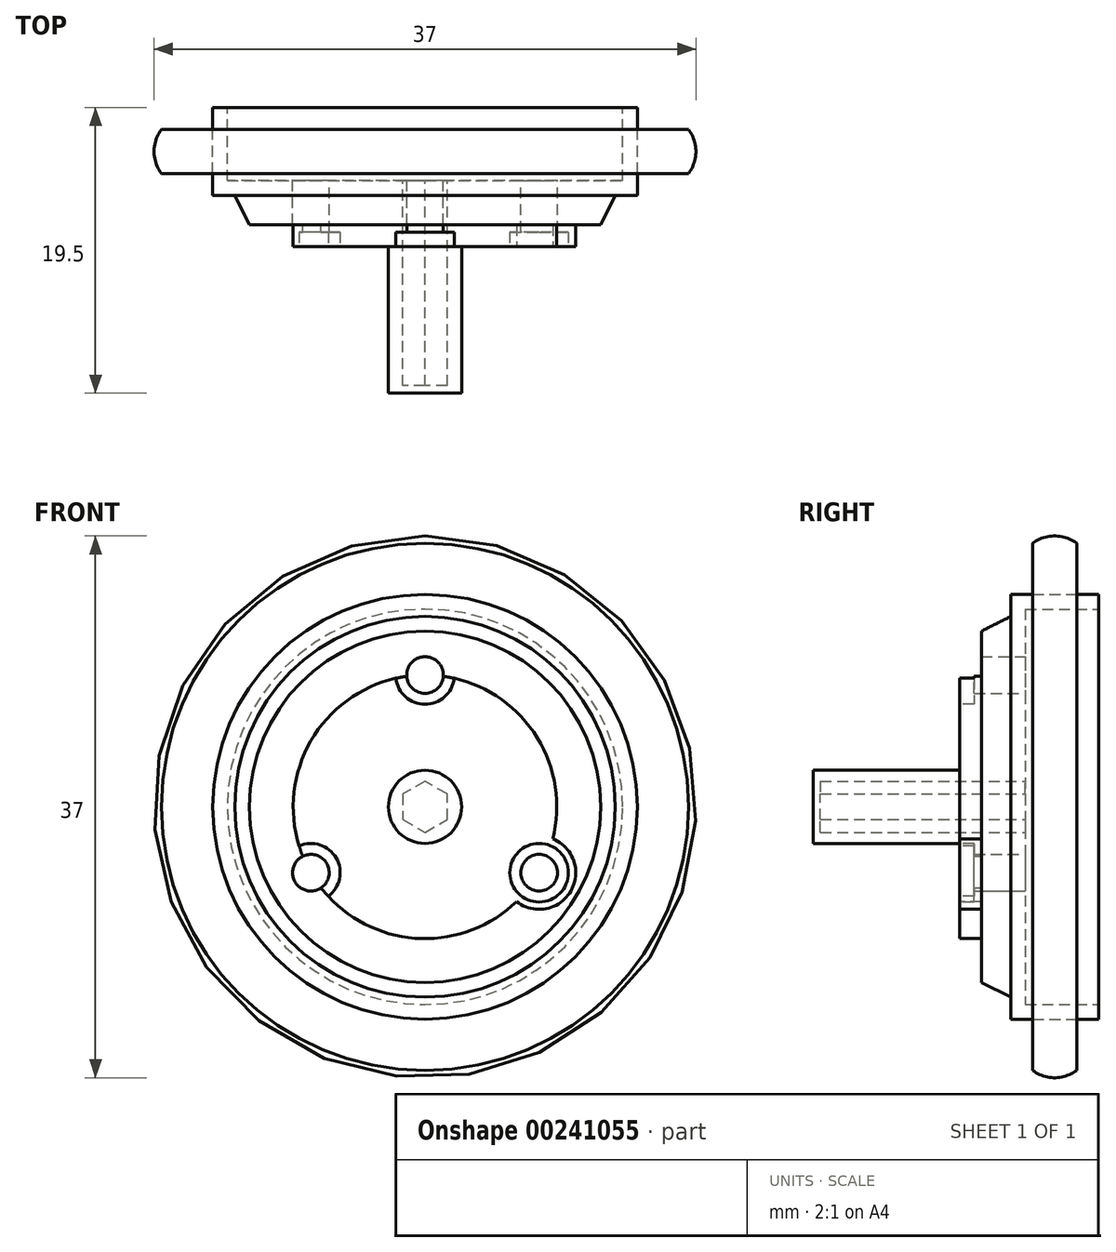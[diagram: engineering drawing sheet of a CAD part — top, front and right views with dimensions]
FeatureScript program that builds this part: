
annotation { "Feature Type Name" : "Feature", "Feature Type Description" : "" }
export const myFeature = defineFeature(function(context is Context, id is Id, definition is map)
    precondition{}
    {
        {
            var Q0;
            Q0=qCreatedBy(makeId("Front.planeOp"),FACE);
            var sketch = newSketch(context, id + "F0", { "sketchPlane" : qUnion([Q0])});
            skCircle(sketch, "E0", {"center": v(0, 0) * mm, "radius": 14.5 * mm});
            skSolve(sketch);
        }
        {
            var Q0;
            Q0=makeQuery(id+"F0.imprint","IMPRINT",FACE,{"disambiguationData":[TD([[makeQuery(id+"F0.imprint","IMPRINT",EDGE,{"derivedFrom":sQuery(id+"F0.wireOp",EDGE,"E0")}),1.0]])]});
            extrude(context, id + "F1", {"entities" : qUnion([Q0]), "depth" : 6 * mm});
        }
        {
            var Q0;
            Q0=qCreatedBy(makeId("Right.planeOp"),FACE);
            var sketch = newSketch(context, id + "F2", { "sketchPlane" : qUnion([Q0])});
            skLineSegment(sketch, "E1.0", {"start": v(-6, -14.5) * mm, "end": v(-6, 14.5) * mm, "construction": true});
            skLineSegment(sketch, "E2", {"start": v(-6, 0) * mm, "end": v(-8, 0) * mm});
            skPoint(sketch, "E2.endSnap0", {"position": v(-6, 0) * mm});
            skLineSegment(sketch, "E3", {"start": v(-8, 0) * mm, "end": v(-8, 12) * mm});
            skLineSegment(sketch, "E4", {"start": v(-8, 12) * mm, "end": v(-6, 13) * mm});
            skLineSegment(sketch, "E5", {"start": v(-6, 13) * mm, "end": v(-6, 0) * mm});
            skSolve(sketch);
        }
        {
            var Q0;
            Q0=makeQuery(id+"F2.imprint","IMPRINT",FACE,{"disambiguationData":[TD([[makeQuery(id+"F2.imprint","IMPRINT",EDGE,{"derivedFrom":sQuery(id+"F2.wireOp",EDGE,"E2")}),-1.0]])]});
            var Q1;
            Q1=sQuery(id+"F2.wireOp",EDGE,"E2");
            revolve(context, id + "F3", {"operationType" : NewBodyOperationType.ADD, "entities" : qUnion([Q0]), "axis" : qUnion([Q1]), "revolveType" : RevolveType.FULL});
        }
        {
            var Q0;
            Q0=makeQuery(id+"F3.opRevolve","SWEPT_FACE",FACE,{"disambiguationData":[OSD([sQuery(id+"F2.wireOp",EDGE,"E3")])]});
            var sketch = newSketch(context, id + "F4", { "sketchPlane" : qUnion([Q0])});
            skCircle(sketch, "E6", {"center": v(0, 0) * mm, "radius": 9 * mm});
            skSolve(sketch);
        }
        {
            var Q0;
            Q0=makeQuery(id+"F4.imprint","IMPRINT",FACE,{"disambiguationData":[TD([[makeQuery(id+"F4.imprint","IMPRINT",EDGE,{"derivedFrom":sQuery(id+"F4.wireOp",EDGE,"E6")}),1.0]])]});
            extrude(context, id + "F5", {"entities" : qUnion([Q0]), "operationType" : NewBodyOperationType.ADD, "depth" : 1.5 * mm});
        }
        {
            var Q0;
            Q0=makeQuery(id+"F5.opExtrude","CAP_FACE",FACE,{"disambiguationData":[OSD([sQuery(id+"F4.wireOp",EDGE,"E6")])],"isStart":false});
            var sketch = newSketch(context, id + "F6", { "sketchPlane" : qUnion([Q0])});
            skCircle(sketch, "E7", {"center": v(0, 0) * mm, "radius": 2.5 * mm});
            skSolve(sketch);
        }
        {
            var Q0;
            Q0=makeQuery(id+"F6.imprint","IMPRINT",FACE,{"disambiguationData":[TD([[makeQuery(id+"F6.imprint","IMPRINT",EDGE,{"derivedFrom":sQuery(id+"F6.wireOp",EDGE,"E7")}),1.0]])]});
            extrude(context, id + "F7", {"entities" : qUnion([Q0]), "operationType" : NewBodyOperationType.ADD, "depth" : 10 * mm});
        }
        {
            var Q0;
            Q0=makeQuery(id+"F5.opExtrude","CAP_FACE",FACE,{"disambiguationData":[OSD([sQuery(id+"F4.wireOp",EDGE,"E6")])],"isStart":false});
            var sketch = newSketch(context, id + "F8", { "sketchPlane" : qUnion([Q0])});
            skCircle(sketch, "E8.0", {"center": v(0, 0) * mm, "radius": 9 * mm, "construction": true});
            skLineSegment(sketch, "E9.0", {"start": v(0, 9) * mm, "end": v(7.8, -4.5) * mm});
            skLineSegment(sketch, "E9.1", {"start": v(7.8, -4.5) * mm, "end": v(-7.8, -4.5) * mm});
            skLineSegment(sketch, "E9.2", {"start": v(-7.8, -4.5) * mm, "end": v(0, 9) * mm});
            skCircle(sketch, "E10", {"center": v(0, 9) * mm, "radius": 2.5 * mm});
            skCircle(sketch, "E11", {"center": v(7.8, -4.5) * mm, "radius": 2.5 * mm});
            skCircle(sketch, "E12", {"center": v(-7.8, -4.5) * mm, "radius": 2.5 * mm});
            skSolve(sketch);
        }
        {
            var Q0;
            {var subQ0=sQuery(id+"F8.wireOp",EDGE,"E9.0");var subQ3=sQuery(id+"F8.wireOp",EDGE,"E11");var subQ4=makeQuery(id+"F8.imprint","INTERSECT",VERTEX,{"derivedFrom":[subQ0,subQ3]});Q0=makeQuery(id+"F8.imprint","IMPRINT",FACE,{"disambiguationData":[TD([[makeQuery(id+"F8.imprint","IMPRINT",EDGE,{"disambiguationData":[TD([[subQ4,1.0]])],"derivedFrom":subQ3}),1.0]])]});}
            var Q1;
            {var subQ0=sQuery(id+"F8.wireOp",EDGE,"E11");var subQ1=makeQuery(id+"F5.opExtrude","CAP_EDGE",EDGE,{"disambiguationData":[OSD([sQuery(id+"F4.wireOp",EDGE,"E6")])],"isStart":false});var subQ2=makeQuery(id+"F8.imprint","INTERSECT",VERTEX,{"disambiguationData":[OD(0.0)],"derivedFrom":[subQ1,subQ0]});Q1=makeQuery(id+"F8.imprint","IMPRINT",FACE,{"disambiguationData":[TD([[makeQuery(id+"F8.imprint","IMPRINT",EDGE,{"disambiguationData":[TD([[subQ2,1.0]])],"derivedFrom":subQ0}),1.0]])]});}
            var Q2;
            {var subQ0=sQuery(id+"F8.wireOp",EDGE,"E9.1");var subQ3=sQuery(id+"F8.wireOp",EDGE,"E11");var subQ4=makeQuery(id+"F8.imprint","INTERSECT",VERTEX,{"derivedFrom":[subQ0,subQ3]});Q2=makeQuery(id+"F8.imprint","IMPRINT",FACE,{"disambiguationData":[TD([[makeQuery(id+"F8.imprint","IMPRINT",EDGE,{"disambiguationData":[TD([[subQ4,-1.0]])],"derivedFrom":subQ3}),1.0]])]});}
            var Q3;
            {var subQ1=sQuery(id+"F8.wireOp",EDGE,"E9.0");var subQ3=sQuery(id+"F8.wireOp",EDGE,"E11");var subQ4=makeQuery(id+"F8.imprint","INTERSECT",VERTEX,{"derivedFrom":[subQ1,subQ3]});Q3=makeQuery(id+"F8.imprint","IMPRINT",FACE,{"disambiguationData":[TD([[makeQuery(id+"F8.imprint","IMPRINT",EDGE,{"disambiguationData":[TD([[subQ4,-1.0]])],"derivedFrom":subQ3}),1.0]])]});}
            var Q4;
            {var subQ1=sQuery(id+"F8.wireOp",EDGE,"E9.1");var subQ3=sQuery(id+"F8.wireOp",EDGE,"E12");var subQ4=makeQuery(id+"F8.imprint","INTERSECT",VERTEX,{"derivedFrom":[subQ1,subQ3]});Q4=makeQuery(id+"F8.imprint","IMPRINT",FACE,{"disambiguationData":[TD([[makeQuery(id+"F8.imprint","IMPRINT",EDGE,{"disambiguationData":[TD([[subQ4,-1.0]])],"derivedFrom":subQ3}),1.0]])]});}
            var Q5;
            {var subQ0=sQuery(id+"F8.wireOp",EDGE,"E9.2");var subQ3=sQuery(id+"F8.wireOp",EDGE,"E12");var subQ4=makeQuery(id+"F8.imprint","INTERSECT",VERTEX,{"derivedFrom":[subQ0,subQ3]});Q5=makeQuery(id+"F8.imprint","IMPRINT",FACE,{"disambiguationData":[TD([[makeQuery(id+"F8.imprint","IMPRINT",EDGE,{"disambiguationData":[TD([[subQ4,-1.0]])],"derivedFrom":subQ3}),1.0]])]});}
            var Q6;
            {var subQ0=sQuery(id+"F8.wireOp",EDGE,"E12");var subQ1=makeQuery(id+"F5.opExtrude","CAP_EDGE",EDGE,{"disambiguationData":[OSD([sQuery(id+"F4.wireOp",EDGE,"E6")])],"isStart":false});var subQ2=makeQuery(id+"F8.imprint","INTERSECT",VERTEX,{"disambiguationData":[OD(0.0)],"derivedFrom":[subQ1,subQ0]});Q6=makeQuery(id+"F8.imprint","IMPRINT",FACE,{"disambiguationData":[TD([[makeQuery(id+"F8.imprint","IMPRINT",EDGE,{"disambiguationData":[TD([[subQ2,-1.0]])],"derivedFrom":subQ0}),1.0]])]});}
            var Q7;
            {var subQ0=sQuery(id+"F8.wireOp",EDGE,"E9.1");var subQ3=sQuery(id+"F8.wireOp",EDGE,"E12");var subQ4=makeQuery(id+"F8.imprint","INTERSECT",VERTEX,{"derivedFrom":[subQ0,subQ3]});Q7=makeQuery(id+"F8.imprint","IMPRINT",FACE,{"disambiguationData":[TD([[makeQuery(id+"F8.imprint","IMPRINT",EDGE,{"disambiguationData":[TD([[subQ4,1.0]])],"derivedFrom":subQ3}),1.0]])]});}
            var Q8;
            {var subQ0=sQuery(id+"F8.wireOp",EDGE,"E9.2");var subQ3=sQuery(id+"F8.wireOp",EDGE,"E10");var subQ4=makeQuery(id+"F8.imprint","INTERSECT",VERTEX,{"derivedFrom":[subQ0,subQ3]});Q8=makeQuery(id+"F8.imprint","IMPRINT",FACE,{"disambiguationData":[TD([[makeQuery(id+"F8.imprint","IMPRINT",EDGE,{"disambiguationData":[TD([[subQ4,1.0]])],"derivedFrom":subQ3}),1.0]])]});}
            var Q9;
            {var subQ1=sQuery(id+"F8.wireOp",EDGE,"E9.0");var subQ3=sQuery(id+"F8.wireOp",EDGE,"E10");var subQ4=makeQuery(id+"F8.imprint","INTERSECT",VERTEX,{"derivedFrom":[subQ1,subQ3]});Q9=makeQuery(id+"F8.imprint","IMPRINT",FACE,{"disambiguationData":[TD([[makeQuery(id+"F8.imprint","IMPRINT",EDGE,{"disambiguationData":[TD([[subQ4,1.0]])],"derivedFrom":subQ3}),1.0]])]});}
            var Q10;
            {var subQ0=sQuery(id+"F8.wireOp",EDGE,"E9.0");var subQ3=sQuery(id+"F8.wireOp",EDGE,"E10");var subQ4=makeQuery(id+"F8.imprint","INTERSECT",VERTEX,{"derivedFrom":[subQ0,subQ3]});Q10=makeQuery(id+"F8.imprint","IMPRINT",FACE,{"disambiguationData":[TD([[makeQuery(id+"F8.imprint","IMPRINT",EDGE,{"disambiguationData":[TD([[subQ4,-1.0]])],"derivedFrom":subQ3}),1.0]])]});}
            var Q11;
            {var subQ0=sQuery(id+"F8.wireOp",EDGE,"E10");var subQ1=makeQuery(id+"F5.opExtrude","CAP_EDGE",EDGE,{"disambiguationData":[OSD([sQuery(id+"F4.wireOp",EDGE,"E6")])],"isStart":false});var subQ2=makeQuery(id+"F8.imprint","INTERSECT",VERTEX,{"disambiguationData":[OD(0.0)],"derivedFrom":[subQ1,subQ0]});Q11=makeQuery(id+"F8.imprint","IMPRINT",FACE,{"disambiguationData":[TD([[makeQuery(id+"F8.imprint","IMPRINT",EDGE,{"disambiguationData":[TD([[subQ2,1.0]])],"derivedFrom":subQ0}),1.0]])]});}
            extrude(context, id + "F9", {"entities" : qUnion([Q0, Q1, Q2, Q3, Q4, Q5, Q6, Q7, Q8, Q9, Q10, Q11]), "operationType" : NewBodyOperationType.ADD, "oppositeDirection" : true, "depth" : 9 * mm});
        }
        {
            var Q0;
            Q0=makeQuery(id+"F1.opExtrude","CAP_FACE",FACE,{"disambiguationData":[OSD([sQuery(id+"F0.wireOp",EDGE,"E0")])],"isStart":true});
            var sketch = newSketch(context, id + "F10", { "sketchPlane" : qUnion([Q0])});
            skCircle(sketch, "E13", {"center": v(0, 0) * mm, "radius": 13.5 * mm});
            skSolve(sketch);
        }
        {
            var Q0;
            Q0=makeQuery(id+"F10.imprint","IMPRINT",FACE,{"disambiguationData":[TD([[makeQuery(id+"F10.imprint","IMPRINT",EDGE,{"derivedFrom":sQuery(id+"F10.wireOp",EDGE,"E13")}),1.0]])]});
            extrude(context, id + "F11", {"entities" : qUnion([Q0]), "operationType" : NewBodyOperationType.REMOVE, "oppositeDirection" : true, "depth" : 5 * mm});
        }
        {
            var Q0;
            Q0=makeQuery(id+"F11.boolean.opBoolean","COPY",FACE,{"derivedFrom":makeQuery(id+"F11.opExtrude","CAP_FACE",FACE,{"disambiguationData":[OSD([sQuery(id+"F10.wireOp",EDGE,"E13")])],"isStart":false})});
            var sketch = newSketch(context, id + "F12", { "sketchPlane" : qUnion([Q0])});
            skCircle(sketch, "E14.cCircle", {"center": v(0, 0) * mm, "radius": 1.75 * mm, "construction": true});
            skLineSegment(sketch, "E14.0", {"start": v(0, 1.75) * mm, "end": v(1.52, 0.88) * mm});
            skLineSegment(sketch, "E14.1", {"start": v(1.52, 0.88) * mm, "end": v(1.52, -0.87) * mm});
            skLineSegment(sketch, "E14.2", {"start": v(1.52, -0.87) * mm, "end": v(0, -1.75) * mm});
            skLineSegment(sketch, "E14.3", {"start": v(0, -1.75) * mm, "end": v(-1.52, -0.88) * mm});
            skLineSegment(sketch, "E14.4", {"start": v(-1.52, -0.88) * mm, "end": v(-1.52, 0.87) * mm});
            skLineSegment(sketch, "E14.5", {"start": v(-1.52, 0.87) * mm, "end": v(0, 1.75) * mm});
            skSolve(sketch);
        }
        {
            var Q0;
            Q0=makeQuery(id+"F12.imprint","IMPRINT",FACE,{"disambiguationData":[TD([[makeQuery(id+"F12.imprint","IMPRINT",EDGE,{"derivedFrom":sQuery(id+"F12.wireOp",EDGE,"E14.0")}),-1.0]])]});
            extrude(context, id + "F13", {"entities" : qUnion([Q0]), "operationType" : NewBodyOperationType.REMOVE, "oppositeDirection" : true, "depth" : 14 * mm});
        }
        {
            var Q0;
            Q0=qCreatedBy(makeId("Top.planeOp"),FACE);
            var sketch = newSketch(context, id + "F14", { "sketchPlane" : qUnion([Q0])});
            skLineSegment(sketch, "E15", {"start": v(14.5, 0) * mm, "end": v(14.5, -6) * mm, "construction": true});
            skLineSegment(sketch, "E16", {"start": v(14.5, -3) * mm, "end": v(14.5, -1.5) * mm});
            skLineSegment(sketch, "E17", {"start": v(14.5, -3) * mm, "end": v(14.5, -4.5) * mm});
            skLineSegment(sketch, "E18", {"start": v(14.5, -1.5) * mm, "end": v(18, -1.5) * mm});
            skLineSegment(sketch, "E19", {"start": v(14.5, -4.5) * mm, "end": v(18, -4.5) * mm});
            skArc(sketch, "E20", {"start": v(18, -4.5) * mm, "mid": v(18.5, -3) * mm, "end": v(18, -1.5) * mm});
            skLineSegment(sketch, "E21.0", {"start": v(14.5, 0) * mm, "end": v(-14.5, 0) * mm, "construction": true});
            skLineSegment(sketch, "E22.0", {"start": v(14.5, -6) * mm, "end": v(-14.5, -6) * mm, "construction": true});
            skLineSegment(sketch, "E23", {"start": v(0, 0) * mm, "end": v(0, -6) * mm, "construction": true});
            skSolve(sketch);
        }
        {
            var Q0;
            Q0=makeQuery(id+"F14.imprint","IMPRINT",FACE,{"disambiguationData":[TD([[makeQuery(id+"F14.imprint","IMPRINT",EDGE,{"derivedFrom":sQuery(id+"F14.wireOp",EDGE,"E16")}),-1.0]])]});
            var Q1;
            Q1=sQuery(id+"F14.wireOp",EDGE,"E23");
            revolve(context, id + "F15", {"entities" : qUnion([Q0]), "axis" : qUnion([Q1]), "revolveType" : RevolveType.FULL});
        }
        {
            var Q0;
            Q0=makeQuery(id+"F9.boolean.opBoolean","MERGE",FACE,{"derivedFrom":[makeQuery(id+"F5.opExtrude","CAP_FACE",FACE,{"disambiguationData":[OSD([sQuery(id+"F4.wireOp",EDGE,"E6")])],"isStart":false}),makeQuery(id+"F9.opExtrude","CAP_FACE",FACE,{"disambiguationData":[OSD([sQuery(id+"F8.wireOp",EDGE,"E10")])],"isStart":true}),makeQuery(id+"F9.opExtrude","CAP_FACE",FACE,{"disambiguationData":[OSD([sQuery(id+"F8.wireOp",EDGE,"E11")])],"isStart":true}),makeQuery(id+"F9.opExtrude","CAP_FACE",FACE,{"disambiguationData":[OSD([sQuery(id+"F8.wireOp",EDGE,"E12")])],"isStart":true})]});
            var sketch = newSketch(context, id + "F16", { "sketchPlane" : qUnion([Q0])});
            skCircle(sketch, "E24", {"center": v(0, 9) * mm, "radius": 2 * mm});
            skCircle(sketch, "E25", {"center": v(7.8, -4.5) * mm, "radius": 2 * mm});
            skCircle(sketch, "E26", {"center": v(-7.8, -4.5) * mm, "radius": 2 * mm});
            skSolve(sketch);
        }
        {
            var Q0;
            Q0=makeQuery(id+"F11.boolean.opBoolean","COPY",FACE,{"derivedFrom":makeQuery(id+"F11.opExtrude","CAP_FACE",FACE,{"disambiguationData":[OSD([sQuery(id+"F10.wireOp",EDGE,"E13")])],"isStart":false})});
            var sketch = newSketch(context, id + "F17", { "sketchPlane" : qUnion([Q0])});
            skSolve(sketch);
        }
        {
            var Q0;
            Q0=makeQuery(id+"F17.imprint","IMPRINT",FACE,{"disambiguationData":[TD([[makeQuery(id+"F17.imprint","IMPRINT",EDGE,{"derivedFrom":makeQuery(id+"F11.boolean.opBoolean","COPY",EDGE,{"derivedFrom":makeQuery(id+"F11.opExtrude","CAP_EDGE",EDGE,{"disambiguationData":[OSD([sQuery(id+"F10.wireOp",EDGE,"E13")])],"isStart":false})})}),1.0]])]});
            var sketch = newSketch(context, id + "F18", { "sketchPlane" : qUnion([Q0])});
            skPoint(sketch, "E27.0", {"position": v(-7.8, -4.5) * mm});
            skPoint(sketch, "E27.1", {"position": v(7.8, -4.5) * mm});
            skPoint(sketch, "E27.2", {"position": v(0, 9) * mm});
            skCircle(sketch, "E28", {"center": v(-7.8, -4.5) * mm, "radius": 1.25 * mm});
            skCircle(sketch, "E29", {"center": v(7.8, -4.5) * mm, "radius": 1.25 * mm});
            skCircle(sketch, "E30", {"center": v(0, 9) * mm, "radius": 1.25 * mm});
            skSolve(sketch);
        }
        {
            var Q0;
            Q0=makeQuery(id+"F18.imprint","IMPRINT",FACE,{"disambiguationData":[TD([[makeQuery(id+"F18.imprint","IMPRINT",EDGE,{"derivedFrom":sQuery(id+"F18.wireOp",EDGE,"E29")}),1.0]])]});
            var Q1;
            Q1=makeQuery(id+"F18.imprint","IMPRINT",FACE,{"disambiguationData":[TD([[makeQuery(id+"F18.imprint","IMPRINT",EDGE,{"derivedFrom":sQuery(id+"F18.wireOp",EDGE,"E30")}),1.0]])]});
            var Q2;
            Q2=makeQuery(id+"F18.imprint","IMPRINT",FACE,{"disambiguationData":[TD([[makeQuery(id+"F18.imprint","IMPRINT",EDGE,{"derivedFrom":sQuery(id+"F18.wireOp",EDGE,"E28")}),1.0]])]});
            var Q3;
            Q3=sQuery(id+"F18.wireOp",EDGE,"E28");
            extrude(context, id + "F19", {"entities" : qUnion([Q0, Q1, Q2]), "operationType" : NewBodyOperationType.REMOVE, "surfaceEntities" : qUnion([Q3]), "oppositeDirection" : true, "depth" : 4.5 * mm});
        }
        {
            var Q0;
            Q0=makeQuery(id+"F16.imprint","IMPRINT",FACE,{"disambiguationData":[TD([[makeQuery(id+"F16.imprint","IMPRINT",EDGE,{"derivedFrom":sQuery(id+"F16.wireOp",EDGE,"E26")}),1.0]])]});
            var Q1;
            Q1=makeQuery(id+"F16.imprint","IMPRINT",FACE,{"disambiguationData":[TD([[makeQuery(id+"F16.imprint","IMPRINT",EDGE,{"derivedFrom":sQuery(id+"F16.wireOp",EDGE,"E25")}),1.0]])]});
            var Q2;
            Q2=makeQuery(id+"F16.imprint","IMPRINT",FACE,{"disambiguationData":[TD([[makeQuery(id+"F16.imprint","IMPRINT",EDGE,{"derivedFrom":sQuery(id+"F16.wireOp",EDGE,"E24")}),1.0]])]});
            extrude(context, id + "F20", {"entities" : qUnion([Q0, Q1, Q2]), "operationType" : NewBodyOperationType.REMOVE, "oppositeDirection" : true, "depth" : 1 * mm});
        }
    });
